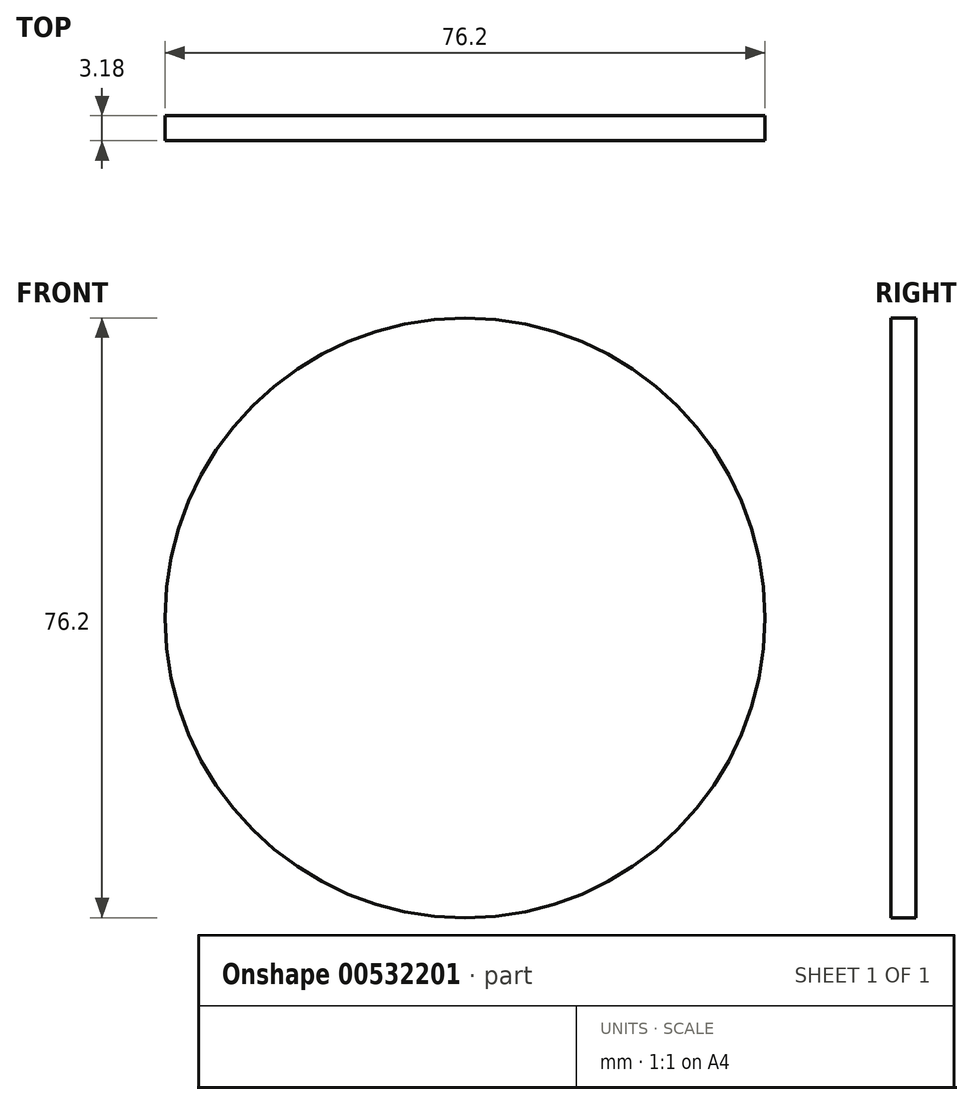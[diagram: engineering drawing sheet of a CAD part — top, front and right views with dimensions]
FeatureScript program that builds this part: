
annotation { "Feature Type Name" : "Feature", "Feature Type Description" : "" }
export const myFeature = defineFeature(function(context is Context, id is Id, definition is map)
    precondition{}
    {
        {
            var Q0;
            Q0=qCreatedBy(makeId("Front.planeOp"),FACE);
            var sketch = newSketch(context, id + "F0", { "sketchPlane" : qUnion([Q0])});
            skCircle(sketch, "E0", {"center": v(0, 0) * mm, "radius": 38.1 * mm});
            skSolve(sketch);
        }
        {
            var Q0;
            Q0 = qSketchRegion(id + "F0", true);
            extrude(context, id + "F1", {"entities" : qUnion([Q0]), "depth" : 3.17 * mm, "offsetDistance" : 25.4 * mm});
        }
    });
